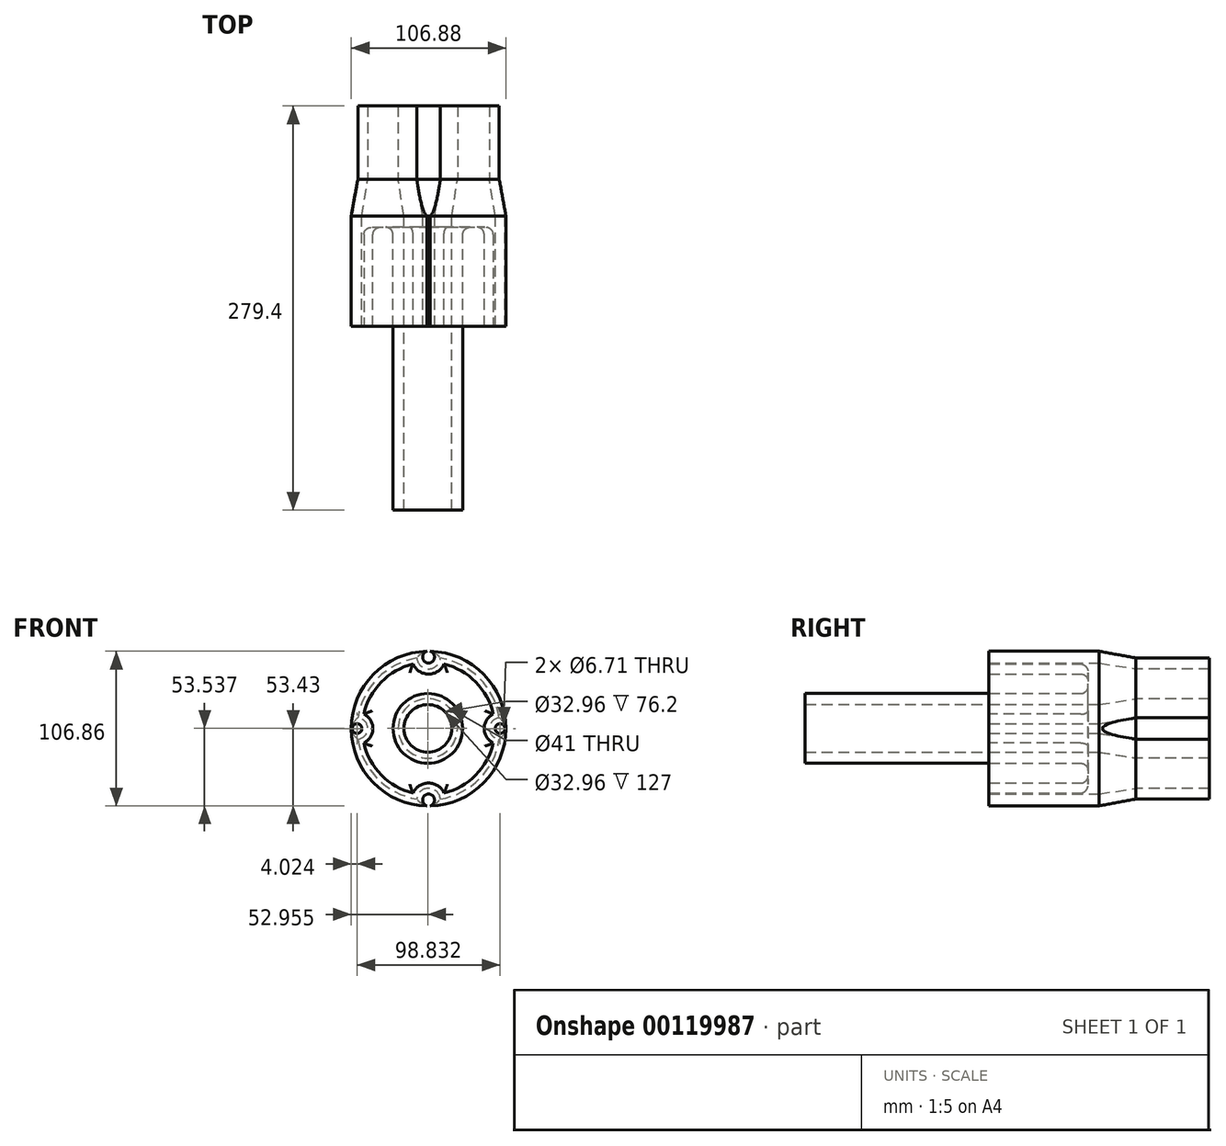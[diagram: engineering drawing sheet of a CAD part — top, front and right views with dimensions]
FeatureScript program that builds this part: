
annotation { "Feature Type Name" : "Feature", "Feature Type Description" : "" }
export const myFeature = defineFeature(function(context is Context, id is Id, definition is map)
    precondition{}
    {
        {
            var Q0;
            Q0=qCreatedBy(makeId("Front.planeOp"),FACE);
            var sketch = newSketch(context, id + "F0", { "sketchPlane" : qUnion([Q0])});
            skLineSegment(sketch, "E0", {"start": v(0, 49.42) * mm, "end": v(0, 49.42) * mm});
            skArc(sketch, "E1", {"start": v(48.87, 7.36) * mm, "mid": v(42.04, 0) * mm, "end": v(48.87, -7.36) * mm});
            skLineSegment(sketch, "E2", {"start": v(88.06, 0) * mm, "end": v(-88.66, 0) * mm, "construction": true});
            skLineSegment(sketch, "E3", {"start": v(0, 85.96) * mm, "end": v(0, -88.97) * mm, "construction": true});
            skArc(sketch, "E4.MirrorC", {"start": v(-48.87, 7.36) * mm, "mid": v(-42.04, 0) * mm, "end": v(-48.87, -7.36) * mm});
            skArc(sketch, "E5.MirrorC", {"start": v(8.14, 48.74) * mm, "mid": v(0, 41.25) * mm, "end": v(-8.14, 48.74) * mm});
            skArc(sketch, "E6.MirrorC", {"start": v(8.14, -48.74) * mm, "mid": v(0, -41.25) * mm, "end": v(-8.14, -48.74) * mm});
            skCircle(sketch, "E7", {"center": v(-0.49, 0.1) * mm, "radius": 20.5 * mm});
            skLineSegment(sketch, "E8.trimOffspring", {"start": v(0, 57.58) * mm, "end": v(0, 57.58) * mm});
            skArc(sketch, "E9.trimOffspring", {"start": v(-8.14, 48.74) * mm, "mid": v(-35.22, 34.66) * mm, "end": v(-48.87, 7.36) * mm});
            skArc(sketch, "E10.trimOffspring", {"start": v(48.87, 7.36) * mm, "mid": v(35.22, 34.66) * mm, "end": v(8.14, 48.74) * mm});
            skLineSegment(sketch, "E11.trimOffspring", {"start": v(0, -57.58) * mm, "end": v(0, -57.58) * mm});
            skLineSegment(sketch, "E12.trimOffspring", {"start": v(0, -49.42) * mm, "end": v(0, -49.42) * mm});
            skArc(sketch, "E13.trimOffspring", {"start": v(8.14, -48.74) * mm, "mid": v(35.22, -34.66) * mm, "end": v(48.87, -7.36) * mm});
            skArc(sketch, "E14.trimOffspring", {"start": v(-48.87, -7.36) * mm, "mid": v(-35.22, -34.66) * mm, "end": v(-8.14, -48.74) * mm});
            skSolve(sketch);
        }
        {
            var Q0;
            Q0=makeQuery(id+"F0.imprint","IMPRINT",FACE,{"disambiguationData":[TD([[makeQuery(id+"F0.imprint","IMPRINT",EDGE,{"derivedFrom":sQuery(id+"F0.wireOp",EDGE,"E1")}),-1.0]])]});
            extrude(context, id + "F3", {"entities" : qUnion([Q0]), "depth" : 25.4 * mm, "hasDraft" : true, "draftAngle" : 9 * degree});
        }
        {
            var Q0;
            Q0=makeQuery(id+"F3.opExtrude","CAP_FACE",FACE,{"disambiguationData":[OSD([sQuery(id+"F0.wireOp",EDGE,"E1"),sQuery(id+"F0.wireOp",EDGE,"E4.MirrorC"),sQuery(id+"F0.wireOp",EDGE,"E5.MirrorC"),sQuery(id+"F0.wireOp",EDGE,"E6.MirrorC"),sQuery(id+"F0.wireOp",EDGE,"E7"),sQuery(id+"F0.wireOp",EDGE,"E9.trimOffspring"),sQuery(id+"F0.wireOp",EDGE,"E10.trimOffspring"),sQuery(id+"F0.wireOp",EDGE,"E13.trimOffspring"),sQuery(id+"F0.wireOp",EDGE,"E14.trimOffspring")])],"isStart":true});
            extrude(context, id + "F4", {"entities" : qUnion([Q0]), "depth" : 50.8 * mm});
        }
        {
            var Q0;
            {var subQ0=sQuery(id+"F0.wireOp",EDGE,"E1");Q0=makeQuery(id+"F3.*.draft.opDraft","MERGE",FACE,{"derivedFrom":[makeQuery(id+"F3.opExtrude","SWEPT_FACE",FACE,{"disambiguationData":[OSD([subQ0])]}),makeQuery(id+"F3.opExtrude","CAP_FACE",FACE,{"disambiguationData":[OSD([subQ0,sQuery(id+"F0.wireOp",EDGE,"E4.MirrorC"),sQuery(id+"F0.wireOp",EDGE,"E5.MirrorC"),sQuery(id+"F0.wireOp",EDGE,"E6.MirrorC"),sQuery(id+"F0.wireOp",EDGE,"E7"),sQuery(id+"F0.wireOp",EDGE,"E9.trimOffspring"),sQuery(id+"F0.wireOp",EDGE,"E10.trimOffspring"),sQuery(id+"F0.wireOp",EDGE,"E13.trimOffspring"),sQuery(id+"F0.wireOp",EDGE,"E14.trimOffspring")])],"isStart":false})]});}
            extrude(context, id + "F1", {"entities" : qUnion([Q0]), "depth" : 76.2 * mm});
        }
        {
            var Q0;
            Q0=makeQuery(id+"F1.opExtrude","CAP_FACE",FACE,{"disambiguationData":[OSD([sQuery(id+"F0.wireOp",EDGE,"E1"),sQuery(id+"F0.wireOp",EDGE,"E4.MirrorC"),sQuery(id+"F0.wireOp",EDGE,"E5.MirrorC"),sQuery(id+"F0.wireOp",EDGE,"E6.MirrorC"),sQuery(id+"F0.wireOp",EDGE,"E7"),sQuery(id+"F0.wireOp",EDGE,"E9.trimOffspring"),sQuery(id+"F0.wireOp",EDGE,"E10.trimOffspring"),sQuery(id+"F0.wireOp",EDGE,"E13.trimOffspring"),sQuery(id+"F0.wireOp",EDGE,"E14.trimOffspring")])],"isStart":false});
            shell(context, id + "F5", {"entities" : qUnion([Q0]), "thickness" : 7.62 * mm});
        }
        {
            var Q0;
            {var subQ0=sQuery(id+"F0.wireOp",EDGE,"E14.trimOffspring");var subQ1=sQuery(id+"F0.wireOp",EDGE,"E13.trimOffspring");var subQ2=sQuery(id+"F0.wireOp",EDGE,"E10.trimOffspring");var subQ3=sQuery(id+"F0.wireOp",EDGE,"E9.trimOffspring");var subQ4=sQuery(id+"F0.wireOp",EDGE,"E7");var subQ5=sQuery(id+"F0.wireOp",EDGE,"E6.MirrorC");var subQ6=sQuery(id+"F0.wireOp",EDGE,"E5.MirrorC");var subQ7=sQuery(id+"F0.wireOp",EDGE,"E4.MirrorC");var subQ8=sQuery(id+"F0.wireOp",EDGE,"E1");Q0=makeQuery(id+"F5.opShell","OFFSET_FACE",FACE,{"disambiguationData":[OSD([subQ8,subQ7,subQ6,subQ5,subQ4,subQ3,subQ2,subQ1,subQ0]),TDD([makeQuery(id+"F1.opExtrude","CAP_FACE",FACE,{"disambiguationData":[OSD([subQ8,subQ7,subQ6,subQ5,subQ4,subQ3,subQ2,subQ1,subQ0])],"isStart":false})])]});}
            extrude(context, id + "F2", {"entities" : qUnion([Q0]), "depth" : 127 * mm});
        }
        {
            var Q0;
            {var subQ0=sQuery(id+"F0.wireOp",EDGE,"E14.trimOffspring");var subQ1=sQuery(id+"F0.wireOp",EDGE,"E13.trimOffspring");var subQ2=sQuery(id+"F0.wireOp",EDGE,"E10.trimOffspring");var subQ3=sQuery(id+"F0.wireOp",EDGE,"E9.trimOffspring");var subQ4=sQuery(id+"F0.wireOp",EDGE,"E7");var subQ5=sQuery(id+"F0.wireOp",EDGE,"E6.MirrorC");var subQ6=sQuery(id+"F0.wireOp",EDGE,"E5.MirrorC");var subQ7=sQuery(id+"F0.wireOp",EDGE,"E4.MirrorC");var subQ8=sQuery(id+"F0.wireOp",EDGE,"E1");Q0=makeQuery(id+"F5.opShell","OFFSET_FACE",FACE,{"disambiguationData":[OSD([subQ8,subQ7,subQ6,subQ5,subQ4,subQ3,subQ2,subQ1,subQ0]),TDD([makeQuery(id+"F1.opExtrude","CAP_FACE",FACE,{"disambiguationData":[OSD([subQ8,subQ7,subQ6,subQ5,subQ4,subQ3,subQ2,subQ1,subQ0])],"isStart":true})])]});}
            fillet(context, id + "F6", {"entities" : qUnion([Q0]), "radius" : 5.08 * mm, "tangentPropagation" : true, "allowEdgeOverflow" : false});
        }
    });
